# Revit family: ewf_ewg-40_60eta2_fta2-hq_50Hz
name_source: partatom
category: 機械設備
units: mm (PartAtom-declared; Revit-internal decimal feet)

## family parameters
OmniClass タイトル = Industrial Ventilating Equipment
OmniClass 番号 = 23.75.35.21.17
パーツ タイプ = 標準
ロード時にボイドで切り取り = はい
丸型コネクタ寸法 = 直径を使用
作業面ベース = いいえ
共有 = いいえ
常に垂直 = はい
部屋計算ポイント = はい

## types (6) — shared parameters
IfcExportAs = IfcFanType
IfcExportType = TUBEAXIAL
MID風量 = 0.0 m³/h
MIN風量 = 0.0 m³/h
OmniClassCode = 23-33 31 19 11 17
URL = https://www.mitsubishielectric.co.jp
Uniclass2015Code = Pr_65_67_29_67
Uniclass2015Title = Propeller fans
Uniclass2015Version = Systems v1.9
ファンの種類 = 軸流羽根
フレームの厚さ = 10  [stored 0.0328084 ft]
仕様書バージョン = Version1.0
企業コード = 108420
分類コード = 50052503100110
周波数 = 50 Hz
呼称 = 有圧扇
極数 = 3
法定耐用年数 = 15
相 = 3
製品リリース年月 = 2022年6月1日
製品出荷対象 = 国内
製造元 = 三菱電機株式会社
設置方法 = 壁付
説明 = 産業用有圧換気扇 低騒音形 耐熱タイプ 給気専用
負荷分類 = 3_ファン類
運転質量 = 0.00 kg

## per-type parameters (varying)
| type | Depth | Height | MAX風量 | Width | オリフィス_Depth | オリフィス径 | モデル | モーター径 | レグ_Depth | レグ_Height | レグ_Width | 価格 | 極 | 消費電力 | 羽根径 | 製品質量 | 質量 | 電動機出力 | 電圧 |
| EWF-40ETA2-HQ_200V | 308  [stored 1.0105 ft] | 520  [stored 1.70604 ft] | 4800.0 m³/h | 520  [stored 1.70604 ft] | 135  [stored 0.442913 ft] | 423  [stored 1.3878 ft] | EWF-40ETA2-HQ | 131  [stored 0.42979 ft] | 279 | 416  [stored 1.36483 ft] | 416  [stored 1.36483 ft] | 203000 $ | 4 | 215 W | ∅400 | 16.70 kg | 20.04 kg | 400 W | 200 V |
| EWF-50FTA2-HQ_200V | 327 | 620  [stored 2.03412 ft] | 6900.0 m³/h | 620  [stored 2.03412 ft] | 155  [stored 0.50853 ft] | 528  [stored 1.73228 ft] | EWF-50FTA2-HQ | 200  [stored 0.656168 ft] | 242  [stored 0.793963 ft] | 516  [stored 1.69291 ft] | 516  [stored 1.69291 ft] | 255000 $ | 4 | 300 W | ∅500 | 25.30 kg | 30.36 kg | 750 W | 200 V |
| EWG-60FTA2-HQ_200V | 375  [stored 1.23031 ft] | 709  [stored 2.32612 ft] | 9420.0 m³/h | 709  [stored 2.32612 ft] | 175  [stored 0.574147 ft] | 624  [stored 2.04724 ft] | EWG-60FTA2-HQ | 200  [stored 0.656168 ft] | 290  [stored 0.951444 ft] | 606  [stored 1.98819 ft] | 606  [stored 1.98819 ft] | 316000 $ | 6 | 385 W | ∅600 | 29.10 kg | 34.92 kg | 750 W | 200 V |
| EWF-40ETA2-HQ_220V | 308  [stored 1.0105 ft] | 520  [stored 1.70604 ft] | 4800.0 m³/h | 520  [stored 1.70604 ft] | 135  [stored 0.442913 ft] | 423  [stored 1.3878 ft] | EWF-40ETA2-HQ | 131  [stored 0.42979 ft] | 279 | 416  [stored 1.36483 ft] | 416  [stored 1.36483 ft] | 203000 $ | 4 | 230 W | ∅400 | 16.70 kg | 20.04 kg | 400 W | 220 V |
| EWF-50FTA2-HQ_220V | 327 | 620  [stored 2.03412 ft] | 6900.0 m³/h | 620  [stored 2.03412 ft] | 155  [stored 0.50853 ft] | 528  [stored 1.73228 ft] | EWF-50FTA2-HQ | 200  [stored 0.656168 ft] | 242  [stored 0.793963 ft] | 516  [stored 1.69291 ft] | 516  [stored 1.69291 ft] | 255000 $ | 4 | 320 W | ∅500 | 25.30 kg | 30.36 kg | 750 W | 220 V |
| EWG-60FTA2-HQ_220V | 375  [stored 1.23031 ft] | 709  [stored 2.32612 ft] | 9420.0 m³/h | 709  [stored 2.32612 ft] | 175  [stored 0.574147 ft] | 624  [stored 2.04724 ft] | EWG-60FTA2-HQ | 200  [stored 0.656168 ft] | 290  [stored 0.951444 ft] | 606  [stored 1.98819 ft] | 606  [stored 1.98819 ft] | 316000 $ | 6 | 400 W | ∅600 | 29.10 kg | 34.92 kg | 750 W | 220 V |

note: [stored X ft] marks values corroborated as IEEE doubles in the binary element streams (Revit-internal decimal feet)
